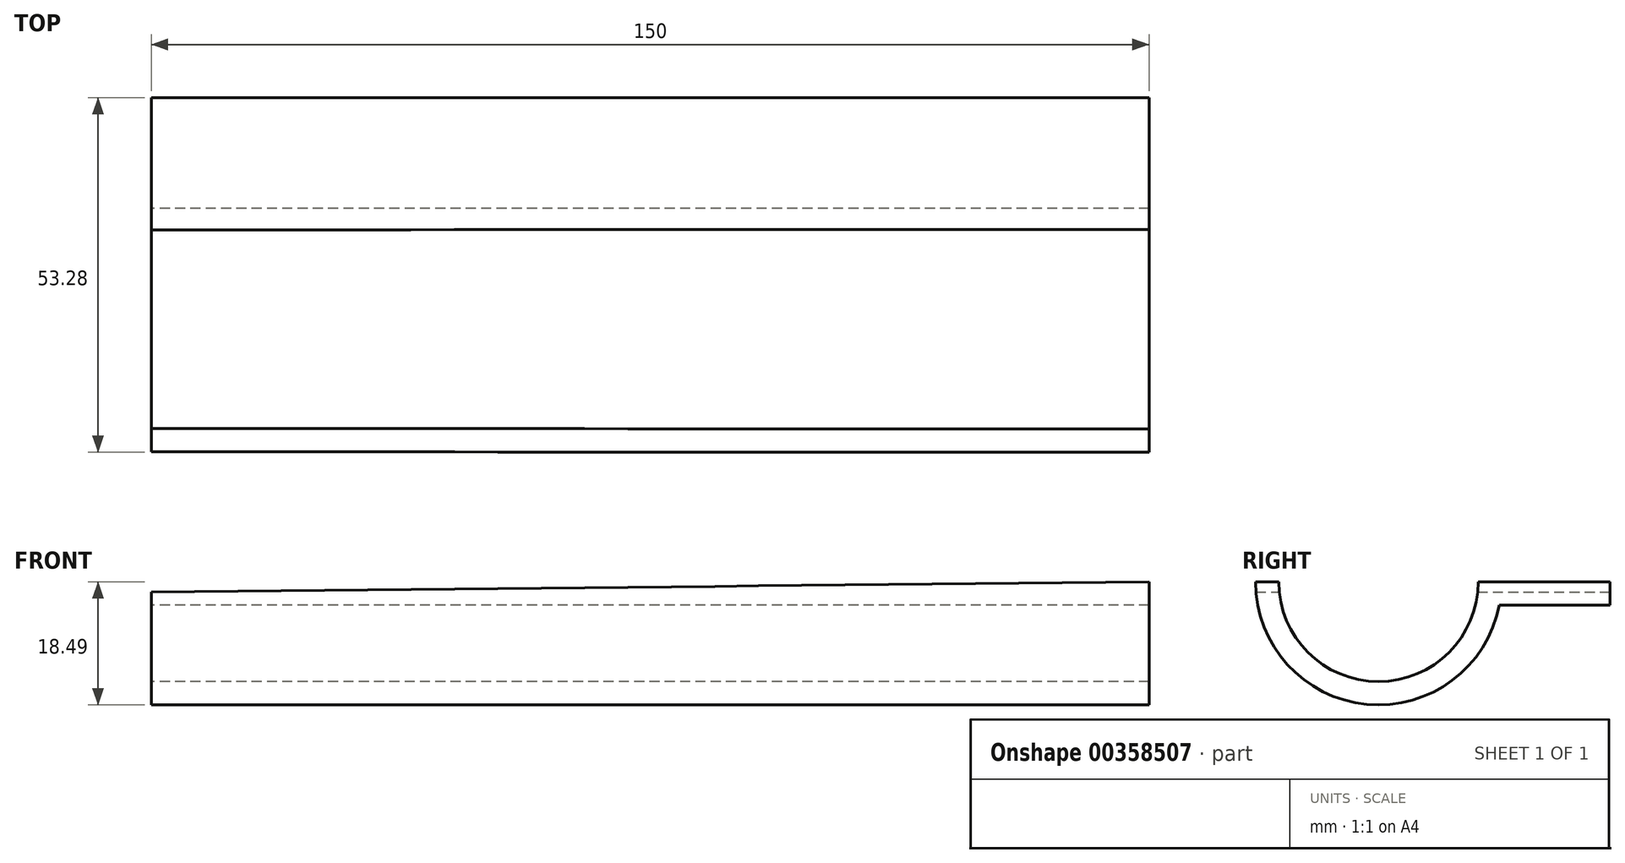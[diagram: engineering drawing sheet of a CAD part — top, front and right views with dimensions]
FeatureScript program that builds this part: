
annotation { "Feature Type Name" : "Feature", "Feature Type Description" : "" }
export const myFeature = defineFeature(function(context is Context, id is Id, definition is map)
    precondition{}
    {
        {
            var Q0;
            Q0=qCreatedBy(makeId("Right.planeOp"),FACE);
            var sketch = newSketch(context, id + "F0", { "sketchPlane" : qUnion([Q0])});
            skArc(sketch, "E0", {"start": v(-116.72, 0) * mm, "mid": v(-101.74, -14.99) * mm, "end": v(-86.75, 0) * mm});
            skPoint(sketch, "E1.orphan", {"position": v(0, 0) * mm});
            skArc(sketch, "E2.0", {"start": v(-120.22, 0) * mm, "mid": v(-103.5, -18.4) * mm, "end": v(-83.58, -3.5) * mm});
            skLineSegment(sketch, "E2.1", {"start": v(-66.94, -3.5) * mm, "end": v(-83.58, -3.5) * mm});
            skLineSegment(sketch, "E3", {"start": v(-66.94, -3.5) * mm, "end": v(-66.94, 0) * mm});
            skLineSegment(sketch, "E4", {"start": v(-116.72, 0) * mm, "end": v(-120.22, 0) * mm});
            skLineSegment(sketch, "E5", {"start": v(-66.94, 0) * mm, "end": v(-86.75, 0) * mm});
            skSolve(sketch);
        }
        {
            var Q0;
            Q0 = qSketchRegion(id + "F0", true);
            extrude(context, id + "F1", {"entities" : qUnion([Q0]), "depth" : 150 * mm});
        }
        {
            var Q0;
            Q0=makeQuery(id+"F1.opExtrude","SWEPT_FACE",FACE,{"disambiguationData":[OSD([sQuery(id+"F0.wireOp",EDGE,"E3")])]});
            var sketch = newSketch(context, id + "F2", { "sketchPlane" : qUnion([Q0])});
            skLineSegment(sketch, "E6.0", {"start": v(-150, 0) * mm, "end": v(0, 0) * mm});
            skPoint(sketch, "E7.0", {"position": v(-150, -1.75) * mm});
            skPoint(sketch, "E8.orphan", {"position": v(-150, -3.5) * mm});
            skLineSegment(sketch, "E9.0", {"start": v(0, -1.75) * mm, "end": v(0, 0) * mm});
            skLineSegment(sketch, "E10", {"start": v(-150, 0) * mm, "end": v(0, -1.53) * mm});
            skPoint(sketch, "E10.endSnap0", {"position": v(0, -1.75) * mm});
            skPoint(sketch, "E11.orphan", {"position": v(0, -3.5) * mm});
            skPoint(sketch, "E12.orphan", {"position": v(21.36, -1.75) * mm});
            skSolve(sketch);
        }
        {
            var Q0;
            Q0 = qSketchRegion(id + "F2", true);
            extrude(context, id + "F3", {"entities" : qUnion([Q0]), "operationType" : NewBodyOperationType.REMOVE, "oppositeDirection" : true, "depth" : 78.74 * mm});
        }
    });
